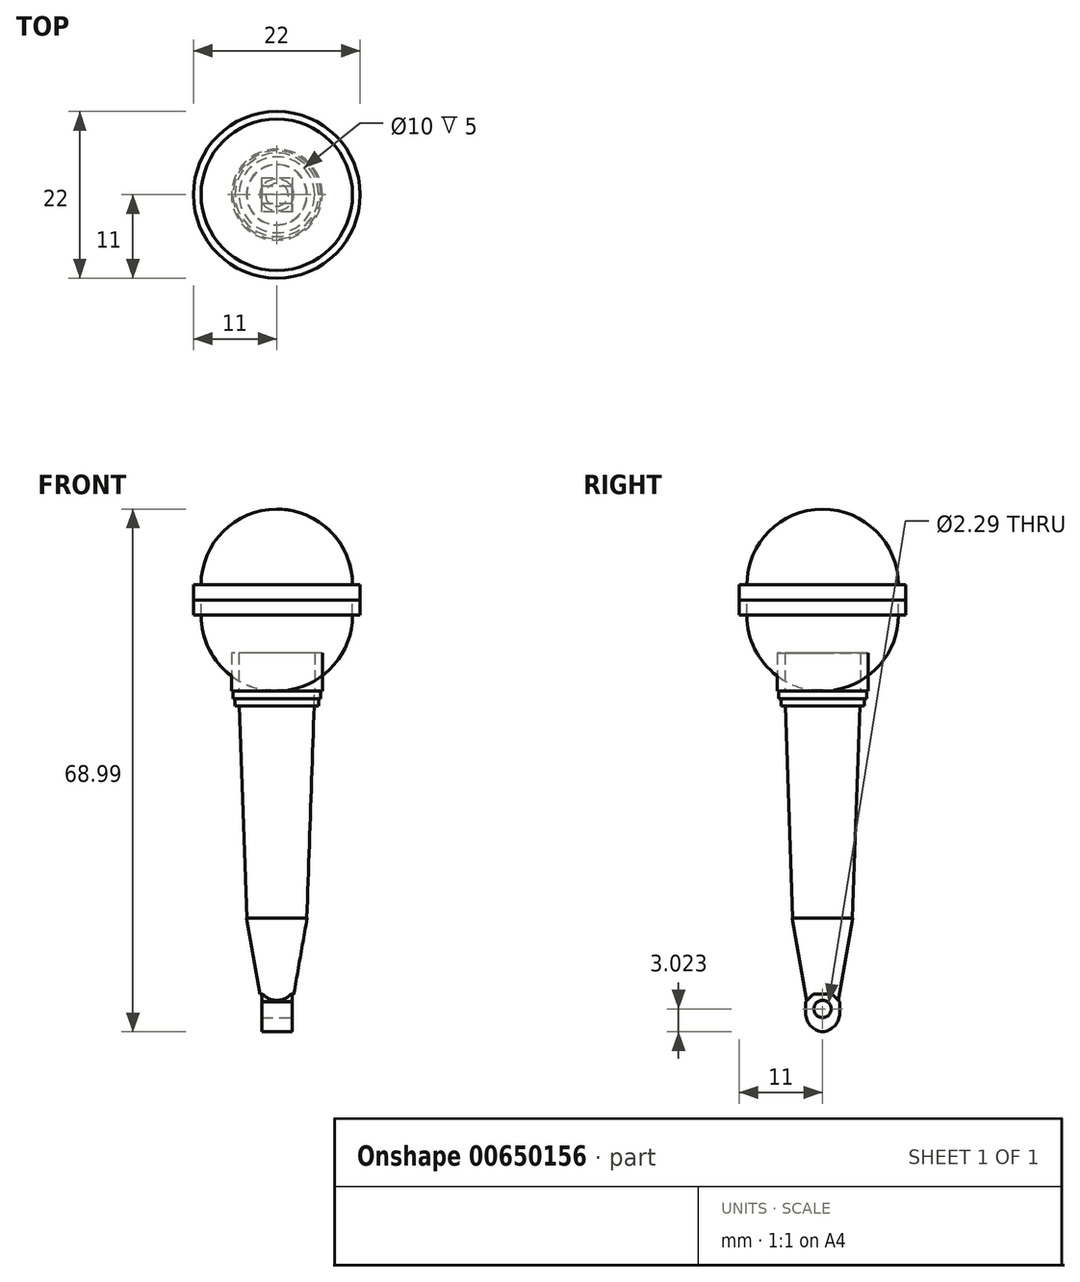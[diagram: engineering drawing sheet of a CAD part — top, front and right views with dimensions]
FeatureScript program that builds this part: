
annotation { "Feature Type Name" : "Feature", "Feature Type Description" : "" }
export const myFeature = defineFeature(function(context is Context, id is Id, definition is map)
    precondition{}
    {
        {
            var Q0;
            Q0=qCreatedBy(makeId("Top.planeOp"),FACE);
            var sketch = newSketch(context, id + "F0", { "sketchPlane" : qUnion([Q0])});
            skCircle(sketch, "E0", {"center": v(0, 0) * mm, "radius": 5 * mm});
            skSolve(sketch);
        }
        {
            var Q0;
            Q0 = qSketchRegion(id + "F0", true);
            extrude(context, id + "F1", {"entities" : qUnion([Q0]), "depth" : 30 * mm, "offsetDistance" : 25 * mm});
        }
        {
            var Q0;
            Q0=makeQuery(id+"F1.opExtrude","CAP_FACE",FACE,{"disambiguationData":[OSD([sQuery(id+"F0.wireOp",EDGE,"E0")])],"isStart":false});
            var sketch = newSketch(context, id + "F2", { "sketchPlane" : qUnion([Q0])});
            skCircle(sketch, "E1", {"center": v(0, 0) * mm, "radius": 6 * mm});
            skSolve(sketch);
        }
        {
            var Q0;
            Q0=makeQuery(id+"F2.imprint","IMPRINT",FACE,{"disambiguationData":[TD([[makeQuery(id+"F2.imprint","IMPRINT",EDGE,{"derivedFrom":sQuery(id+"F2.wireOp",EDGE,"E1")}),1.0]])]});
            extrude(context, id + "F3", {"entities" : qUnion([Q0]), "depth" : 5 * mm, "offsetDistance" : 25 * mm});
        }
        {
            var Q0;
            Q0=makeQuery(id+"F1.opExtrude","CAP_FACE",FACE,{"disambiguationData":[OSD([sQuery(id+"F0.wireOp",EDGE,"E0")])],"isStart":false});
            var sketch = newSketch(context, id + "F4", { "sketchPlane" : qUnion([Q0])});
            skCircle(sketch, "E2", {"center": v(0, 0) * mm, "radius": 3.5 * mm});
            skSolve(sketch);
        }
        {
            var Q0;
            Q0 = qSketchRegion(id + "F4", true);
            extrude(context, id + "F5", {"entities" : qUnion([Q0]), "operationType" : NewBodyOperationType.ADD, "depth" : -3 * mm, "offsetDistance" : 25 * mm});
        }
        {
            var Q0;
            Q0=makeQuery(id+"F5.boolean.opBoolean","MERGE",FACE,{"derivedFrom":[makeQuery(id+"F1.opExtrude","CAP_FACE",FACE,{"disambiguationData":[OSD([sQuery(id+"F0.wireOp",EDGE,"E0")])],"isStart":false}),makeQuery(id+"F5.opExtrude","CAP_FACE",FACE,{"disambiguationData":[OSD([sQuery(id+"F4.wireOp",EDGE,"E2")])],"isStart":true})]});
            var sketch = newSketch(context, id + "F6", { "sketchPlane" : qUnion([Q0])});
            skCircle(sketch, "E3", {"center": v(0, 0) * mm, "radius": 1.5 * mm});
            skSolve(sketch);
        }
        {
            var Q0;
            Q0=makeQuery(id+"F6.imprint","IMPRINT",FACE,{"disambiguationData":[TD([[makeQuery(id+"F6.imprint","IMPRINT",EDGE,{"derivedFrom":sQuery(id+"F6.wireOp",EDGE,"E3")}),1.0]])]});
            extrude(context, id + "F7", {"entities" : qUnion([Q0]), "operationType" : NewBodyOperationType.ADD, "depth" : 12 * mm, "offsetDistance" : 25 * mm});
        }
        {
            var Q0;
            Q0=makeQuery(id+"F5.boolean.opBoolean","MERGE",FACE,{"derivedFrom":[makeQuery(id+"F1.opExtrude","CAP_FACE",FACE,{"disambiguationData":[OSD([sQuery(id+"F0.wireOp",EDGE,"E0")])],"isStart":false}),makeQuery(id+"F5.opExtrude","CAP_FACE",FACE,{"disambiguationData":[OSD([sQuery(id+"F4.wireOp",EDGE,"E2")])],"isStart":true})]});
            var sketch = newSketch(context, id + "F8", { "sketchPlane" : qUnion([Q0])});
            skLineSegment(sketch, "E4.bottom", {"start": v(-10, 10) * mm, "end": v(10, 10) * mm});
            skLineSegment(sketch, "E4.top", {"start": v(-10, -10) * mm, "end": v(10, -10) * mm});
            skLineSegment(sketch, "E4.left", {"start": v(-10, 10) * mm, "end": v(-10, -10) * mm});
            skLineSegment(sketch, "E4.right", {"start": v(10, 10) * mm, "end": v(10, -10) * mm});
            skPoint(sketch, "E4.middle", {"position": v(0, 0) * mm});
            skSolve(sketch);
        }
        {
            var Q0;
            Q0 = qSketchRegion(id + "F8", true);
            extrude(context, id + "F9", {"entities" : qUnion([Q0]), "depth" : 24 * mm, "offsetDistance" : 25 * mm});
        }
        {
            var Q0;
            Q0=makeQuery(id+"F9.opExtrude","CAP_EDGE",EDGE,{"disambiguationData":[OSD([sQuery(id+"F8.wireOp",EDGE,"E4.bottom")])],"isStart":false});
            var Q1;
            Q1=makeQuery(id+"F9.opExtrude","CAP_EDGE",EDGE,{"disambiguationData":[OSD([sQuery(id+"F8.wireOp",EDGE,"E4.right")])],"isStart":false});
            var Q2;
            Q2=makeQuery(id+"F9.opExtrude","CAP_EDGE",EDGE,{"disambiguationData":[OSD([sQuery(id+"F8.wireOp",EDGE,"E4.top")])],"isStart":false});
            var Q3;
            Q3=makeQuery(id+"F9.opExtrude","CAP_EDGE",EDGE,{"disambiguationData":[OSD([sQuery(id+"F8.wireOp",EDGE,"E4.left")])],"isStart":false});
            var Q4;
            Q4=makeQuery(id+"F9.opExtrude","CAP_EDGE",EDGE,{"disambiguationData":[OSD([sQuery(id+"F8.wireOp",EDGE,"E4.top")])],"isStart":true});
            var Q5;
            Q5=makeQuery(id+"F9.opExtrude","CAP_EDGE",EDGE,{"disambiguationData":[OSD([sQuery(id+"F8.wireOp",EDGE,"E4.left")])],"isStart":true});
            var Q6;
            Q6=makeQuery(id+"F9.opExtrude","CAP_EDGE",EDGE,{"disambiguationData":[OSD([sQuery(id+"F8.wireOp",EDGE,"E4.bottom")])],"isStart":true});
            var Q7;
            Q7=makeQuery(id+"F9.opExtrude","CAP_EDGE",EDGE,{"disambiguationData":[OSD([sQuery(id+"F8.wireOp",EDGE,"E4.right")])],"isStart":true});
            var Q8;
            Q8=makeQuery(id+"F9.opExtrude","SWEPT_EDGE",EDGE,{"disambiguationData":[OSD([sQuery(id+"F8.wireOp",EDGE,"E4.bottom"),sQuery(id+"F8.wireOp",EDGE,"E4.right")])]});
            var Q9;
            Q9=makeQuery(id+"F9.opExtrude","SWEPT_EDGE",EDGE,{"disambiguationData":[OSD([sQuery(id+"F8.wireOp",EDGE,"E4.top"),sQuery(id+"F8.wireOp",EDGE,"E4.right")])]});
            var Q10;
            Q10=makeQuery(id+"F9.opExtrude","SWEPT_EDGE",EDGE,{"disambiguationData":[OSD([sQuery(id+"F8.wireOp",EDGE,"E4.top"),sQuery(id+"F8.wireOp",EDGE,"E4.left")])]});
            var Q11;
            Q11=makeQuery(id+"F9.opExtrude","SWEPT_EDGE",EDGE,{"disambiguationData":[OSD([sQuery(id+"F8.wireOp",EDGE,"E4.bottom"),sQuery(id+"F8.wireOp",EDGE,"E4.left")])]});
            fillet(context, id + "F10", {"entities" : qUnion([Q0, Q1, Q2, Q3, Q4, Q5, Q6, Q7, Q8, Q9, Q10, Q11]), "radius" : 10 * mm, "tangentPropagation" : true, "allowEdgeOverflow" : false});
        }
        {
            var Q0;
            Q0=makeQuery(id+"F7.opExtrude","CAP_FACE",FACE,{"disambiguationData":[OSD([sQuery(id+"F6.wireOp",EDGE,"E3")])],"isStart":false});
            var sketch = newSketch(context, id + "F11", { "sketchPlane" : qUnion([Q0])});
            skCircle(sketch, "E5", {"center": v(0, 0) * mm, "radius": 11 * mm});
            skSolve(sketch);
        }
        {
            var Q0;
            Q0 = qSketchRegion(id + "F11", true);
            extrude(context, id + "F12", {"entities" : qUnion([Q0]), "operationType" : NewBodyOperationType.ADD, "depth" : 2 * mm, "offsetDistance" : 25 * mm});
        }
        {
            var Q0;
            Q0 = qSketchRegion(id + "F11", true);
            extrude(context, id + "F13", {"entities" : qUnion([Q0]), "depth" : -2 * mm, "offsetDistance" : 25 * mm});
        }
        {
            var Q0;
            Q0=makeQuery(id+"F3.opExtrude","CAP_FACE",FACE,{"disambiguationData":[OSD([sQuery(id+"F0.wireOp",EDGE,"E0"),sQuery(id+"F2.wireOp",EDGE,"E1")])],"isStart":true});
            var sketch = newSketch(context, id + "F14", { "sketchPlane" : qUnion([Q0])});
            skCircle(sketch, "E6", {"center": v(0, 0) * mm, "radius": 5.8 * mm});
            skSolve(sketch);
        }
        {
            var Q0;
            Q0 = qSketchRegion(id + "F14", true);
            extrude(context, id + "F15", {"entities" : qUnion([Q0]), "depth" : 1 * mm, "offsetDistance" : 25 * mm});
        }
        {
            var Q0;
            Q0=makeQuery(id+"F15.opExtrude","CAP_FACE",FACE,{"disambiguationData":[OSD([sQuery(id+"F14.wireOp",EDGE,"E6")])],"isStart":false});
            var sketch = newSketch(context, id + "F16", { "sketchPlane" : qUnion([Q0])});
            skCircle(sketch, "E7", {"center": v(0, 0) * mm, "radius": 5.5 * mm});
            skSolve(sketch);
        }
        {
            var Q0;
            Q0 = qSketchRegion(id + "F16", true);
            extrude(context, id + "F17", {"entities" : qUnion([Q0]), "depth" : 1 * mm, "offsetDistance" : 25 * mm});
        }
        {
            var Q0;
            Q0=qCreatedBy(makeId("Top.planeOp"),FACE);
            var sketch = newSketch(context, id + "F18", { "sketchPlane" : qUnion([Q0])});
            skCircle(sketch, "E8", {"center": v(0, 0) * mm, "radius": 4 * mm});
            skCircle(sketch, "E9", {"center": v(0, 0) * mm, "radius": 3.5 * mm});
            skSolve(sketch);
        }
        {
            var Q0;
            Q0=makeQuery(id+"F1.opExtrude","CAP_EDGE",EDGE,{"disambiguationData":[OSD([sQuery(id+"F0.wireOp",EDGE,"E0")])],"isStart":true});
            chamfer(context, id + "F19", {"entities" : qUnion([Q0]), "chamferType" : ChamferType.OFFSET_ANGLE, "width" : 30 * mm, "oppositeDirection" : false, "angle" : 2 * degree, "tangentPropagation" : true});
        }
        {
            var Q0;
            Q0=makeQuery(id+"F18.imprint","IMPRINT",FACE,{"disambiguationData":[TD([[makeQuery(id+"F18.imprint","IMPRINT",EDGE,{"derivedFrom":sQuery(id+"F18.wireOp",EDGE,"E9")}),1.0]])]});
            var sketch = newSketch(context, id + "F20", { "sketchPlane" : qUnion([Q0])});
            skCircle(sketch, "E10", {"center": v(0, 0) * mm, "radius": 4 * mm});
            skSolve(sketch);
        }
        {
            var Q0;
            Q0 = qSketchRegion(id + "F20", true);
            extrude(context, id + "F21", {"entities" : qUnion([Q0]), "operationType" : NewBodyOperationType.ADD, "depth" : -10 * mm, "offsetDistance" : 25 * mm});
        }
        {
            var Q0;
            Q0=makeQuery(id+"F21.opExtrude","CAP_EDGE",EDGE,{"disambiguationData":[OSD([sQuery(id+"F20.wireOp",EDGE,"E10")])],"isStart":false});
            chamfer(context, id + "F22", {"entities" : qUnion([Q0]), "chamferType" : ChamferType.OFFSET_ANGLE, "width" : 10 * mm, "oppositeDirection" : false, "angle" : 10 * degree, "tangentPropagation" : true});
        }
        {
            var Q0;
            Q0=makeQuery(id+"F21.opExtrude","CAP_FACE",FACE,{"disambiguationData":[OSD([sQuery(id+"F20.wireOp",EDGE,"E10")])],"isStart":false});
            var sketch = newSketch(context, id + "F23", { "sketchPlane" : qUnion([Q0])});
            skLineSegment(sketch, "E11", {"start": v(0, -2.24) * mm, "end": v(0, 2.24) * mm});
            skPoint(sketch, "E12.middle", {"position": v(0, 0) * mm});
            skLineSegment(sketch, "E13", {"start": v(0, 2.24) * mm, "end": v(2, 2.24) * mm});
            skLineSegment(sketch, "E14.bottom", {"start": v(2, 2.24) * mm, "end": v(-2, 2.24) * mm});
            skLineSegment(sketch, "E14.top", {"start": v(2, -2.26) * mm, "end": v(-2, -2.26) * mm});
            skLineSegment(sketch, "E14.left", {"start": v(2, 2.24) * mm, "end": v(2, -2.26) * mm});
            skLineSegment(sketch, "E14.right", {"start": v(-2, 2.24) * mm, "end": v(-2, -2.26) * mm});
            skSolve(sketch);
        }
        {
            var Q0;
            Q0 = qSketchRegion(id + "F23", true);
            extrude(context, id + "F24", {"entities" : qUnion([Q0]), "operationType" : NewBodyOperationType.ADD, "depth" : 5 * mm, "offsetDistance" : 25 * mm});
        }
        {
            var Q0;
            Q0=makeQuery(id+"F24.opExtrude","CAP_EDGE",EDGE,{"disambiguationData":[OSD([sQuery(id+"F23.wireOp",EDGE,"E14.top")])],"isStart":false});
            var Q1;
            Q1=makeQuery(id+"F24.opExtrude","CAP_EDGE",EDGE,{"disambiguationData":[OSD([sQuery(id+"F23.wireOp",EDGE,"E14.bottom")])],"isStart":false});
            fillet(context, id + "F25", {"entities" : qUnion([Q0, Q1]), "radius" : 2.5 * mm, "tangentPropagation" : true, "allowEdgeOverflow" : false});
        }
        {
            var Q0;
            Q0=makeQuery(id+"F24.opExtrude","CAP_EDGE",EDGE,{"disambiguationData":[OSD([sQuery(id+"F23.wireOp",EDGE,"E14.top")])],"isStart":true});
            var Q1;
            {var subQ0=sQuery(id+"F23.wireOp",EDGE,"E14.bottom");var subQ1=sQuery(id+"F23.wireOp",EDGE,"E14.left");Q1=makeQuery(id+"F24.boolean.opBoolean","SPLIT",EDGE,{"disambiguationData":[TD([makeQuery(id+"F24.opExtrude","SWEPT_FACE",FACE,{"disambiguationData":[OSD([subQ1])]})])],"derivedFrom":makeQuery(id+"F24.opExtrude","CAP_EDGE",EDGE,{"disambiguationData":[OSD([subQ0])],"isStart":true})});}
            chamfer(context, id + "F26", {"entities" : qUnion([Q0, Q1]), "width" : 1 * mm, "tangentPropagation" : true});
        }
        {
            var Q0;
            Q0=makeQuery(id+"F24.opExtrude","SWEPT_FACE",FACE,{"disambiguationData":[OSD([sQuery(id+"F23.wireOp",EDGE,"E14.left")])]});
            var sketch = newSketch(context, id + "F27", { "sketchPlane" : qUnion([Q0])});
            skCircle(sketch, "E15", {"center": v(0, -11.97) * mm, "radius": 1.15 * mm});
            skSolve(sketch);
        }
        {
            var Q0;
            Q0=makeQuery(id+"F27.imprint","IMPRINT",FACE,{"disambiguationData":[TD([[makeQuery(id+"F27.imprint","IMPRINT",EDGE,{"derivedFrom":sQuery(id+"F27.wireOp",EDGE,"E15")}),1.0]])]});
            extrude(context, id + "F28", {"entities" : qUnion([Q0]), "operationType" : NewBodyOperationType.REMOVE, "oppositeDirection" : true, "depth" : 25 * mm, "offsetDistance" : 25 * mm});
        }
    });
